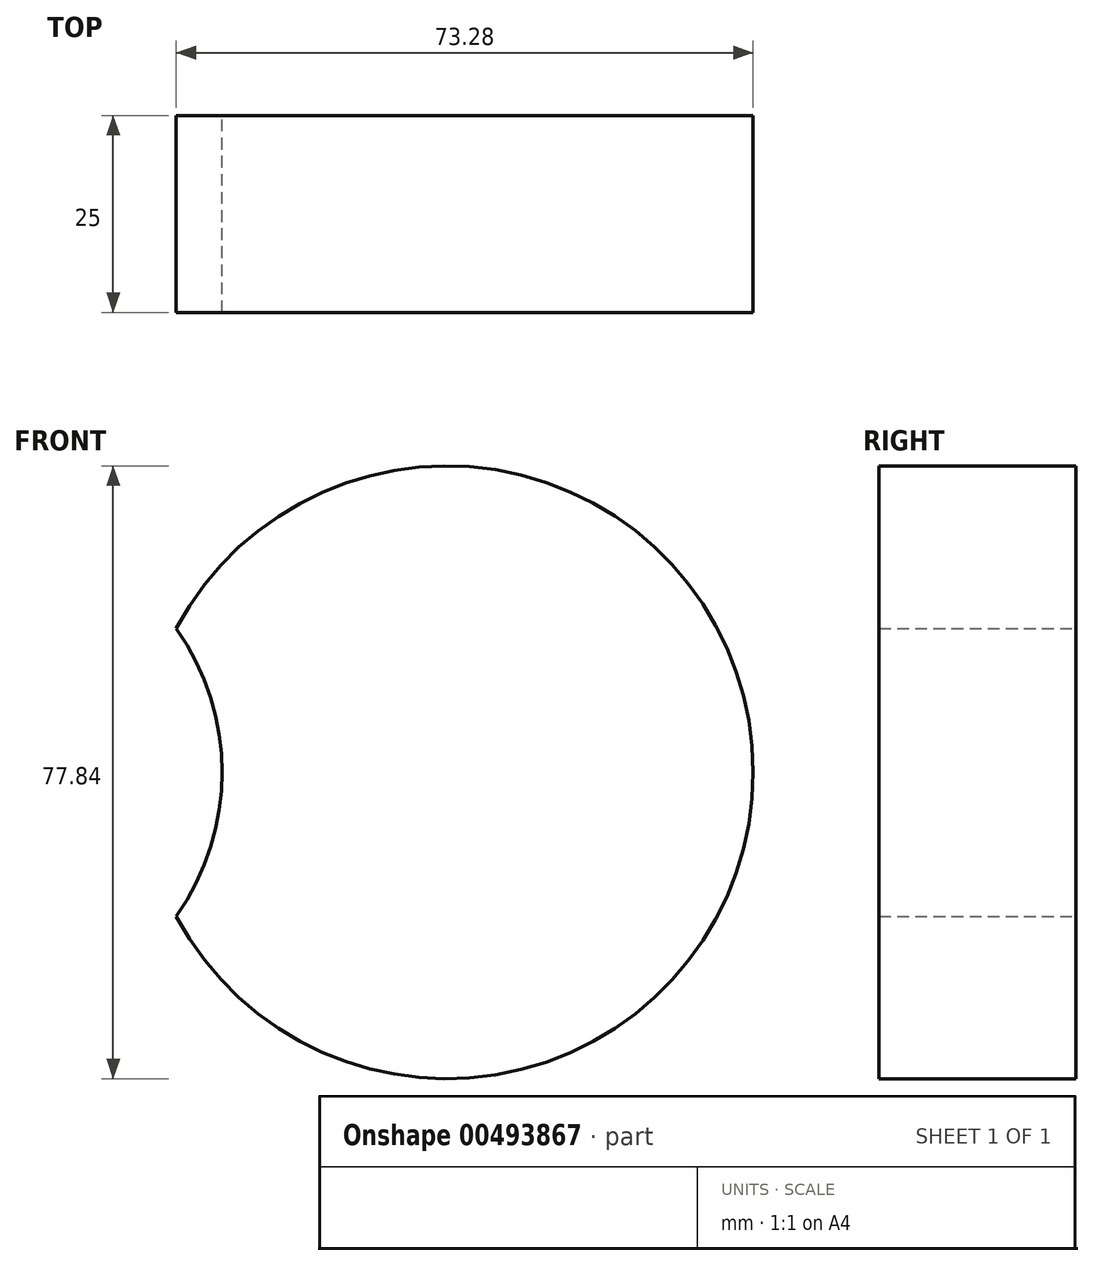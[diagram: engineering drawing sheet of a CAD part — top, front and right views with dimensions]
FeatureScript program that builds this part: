
annotation { "Feature Type Name" : "Feature", "Feature Type Description" : "" }
export const myFeature = defineFeature(function(context is Context, id is Id, definition is map)
    precondition{}
    {
        {
            var Q0;
            Q0=qCreatedBy(makeId("Front.planeOp"),FACE);
            var sketch = newSketch(context, id + "F0", { "sketchPlane" : qUnion([Q0])});
            skCircle(sketch, "E0", {"center": v(-40.57, 0) * mm, "radius": 31.63 * mm});
            skCircle(sketch, "E1", {"center": v(19.6, 0) * mm, "radius": 38.92 * mm});
            skSolve(sketch);
        }
        {
            var Q0;
            {var subQ0=sQuery(id+"F0.wireOp",EDGE,"E1");var subQ1=sQuery(id+"F0.wireOp",EDGE,"E0");var subQ2=makeQuery(id+"F0.imprint","INTERSECT",VERTEX,{"disambiguationData":[OD(0.0)],"derivedFrom":[subQ1,subQ0]});Q0=makeQuery(id+"F0.imprint","IMPRINT",FACE,{"disambiguationData":[TD([[makeQuery(id+"F0.imprint","IMPRINT",EDGE,{"disambiguationData":[TD([[subQ2,1.0]])],"derivedFrom":subQ1}),1.0]])]});}
            var Q1;
            {var subQ0=sQuery(id+"F0.wireOp",EDGE,"E1");var subQ1=sQuery(id+"F0.wireOp",EDGE,"E0");var subQ2=makeQuery(id+"F0.imprint","INTERSECT",VERTEX,{"disambiguationData":[OD(0.0)],"derivedFrom":[subQ1,subQ0]});Q1=makeQuery(id+"F0.imprint","IMPRINT",FACE,{"disambiguationData":[TD([[makeQuery(id+"F0.imprint","IMPRINT",EDGE,{"disambiguationData":[TD([[subQ2,-1.0]])],"derivedFrom":subQ1}),1.0]])]});}
            extrude(context, id + "F1", {"entities" : qUnion([Q0, Q1]), "depth" : 25 * mm});
        }
        {
            var Q0;
            {var subQ0=sQuery(id+"F0.wireOp",EDGE,"E1");var subQ1=sQuery(id+"F0.wireOp",EDGE,"E0");var subQ2=makeQuery(id+"F0.imprint","INTERSECT",VERTEX,{"disambiguationData":[OD(0.0)],"derivedFrom":[subQ1,subQ0]});Q0=makeQuery(id+"F0.imprint","IMPRINT",FACE,{"disambiguationData":[TD([[makeQuery(id+"F0.imprint","IMPRINT",EDGE,{"disambiguationData":[TD([[subQ2,-1.0]])],"derivedFrom":subQ1}),-1.0]])]});}
            var Q1;
            {var subQ0=sQuery(id+"F0.wireOp",EDGE,"E1");var subQ1=sQuery(id+"F0.wireOp",EDGE,"E0");var subQ2=makeQuery(id+"F0.imprint","INTERSECT",VERTEX,{"disambiguationData":[OD(0.0)],"derivedFrom":[subQ1,subQ0]});Q1=makeQuery(id+"F0.imprint","IMPRINT",FACE,{"disambiguationData":[TD([[makeQuery(id+"F0.imprint","IMPRINT",EDGE,{"disambiguationData":[TD([[subQ2,-1.0]])],"derivedFrom":subQ1}),1.0]])]});}
            extrude(context, id + "F2", {"entities" : qUnion([Q0, Q1]), "depth" : 25 * mm});
        }
        {
            var Q0;
            Q0=makeQuery(id+"F1.opExtrude","SWEPT_BODY",BODY,{"disambiguationData":[OSD([sQuery(id+"F0.wireOp",EDGE,"E0")])]});
            var Q1;
            Q1=makeQuery(id+"F2.opExtrude","SWEPT_BODY",BODY,{"disambiguationData":[OSD([sQuery(id+"F0.wireOp",EDGE,"E1")])]});
            booleanBodies(context, id + "F3", {"operationType" : BooleanOperationType.SUBTRACTION, "tools" : qUnion([Q0]), "targets" : qUnion([Q1])});
        }
    });
